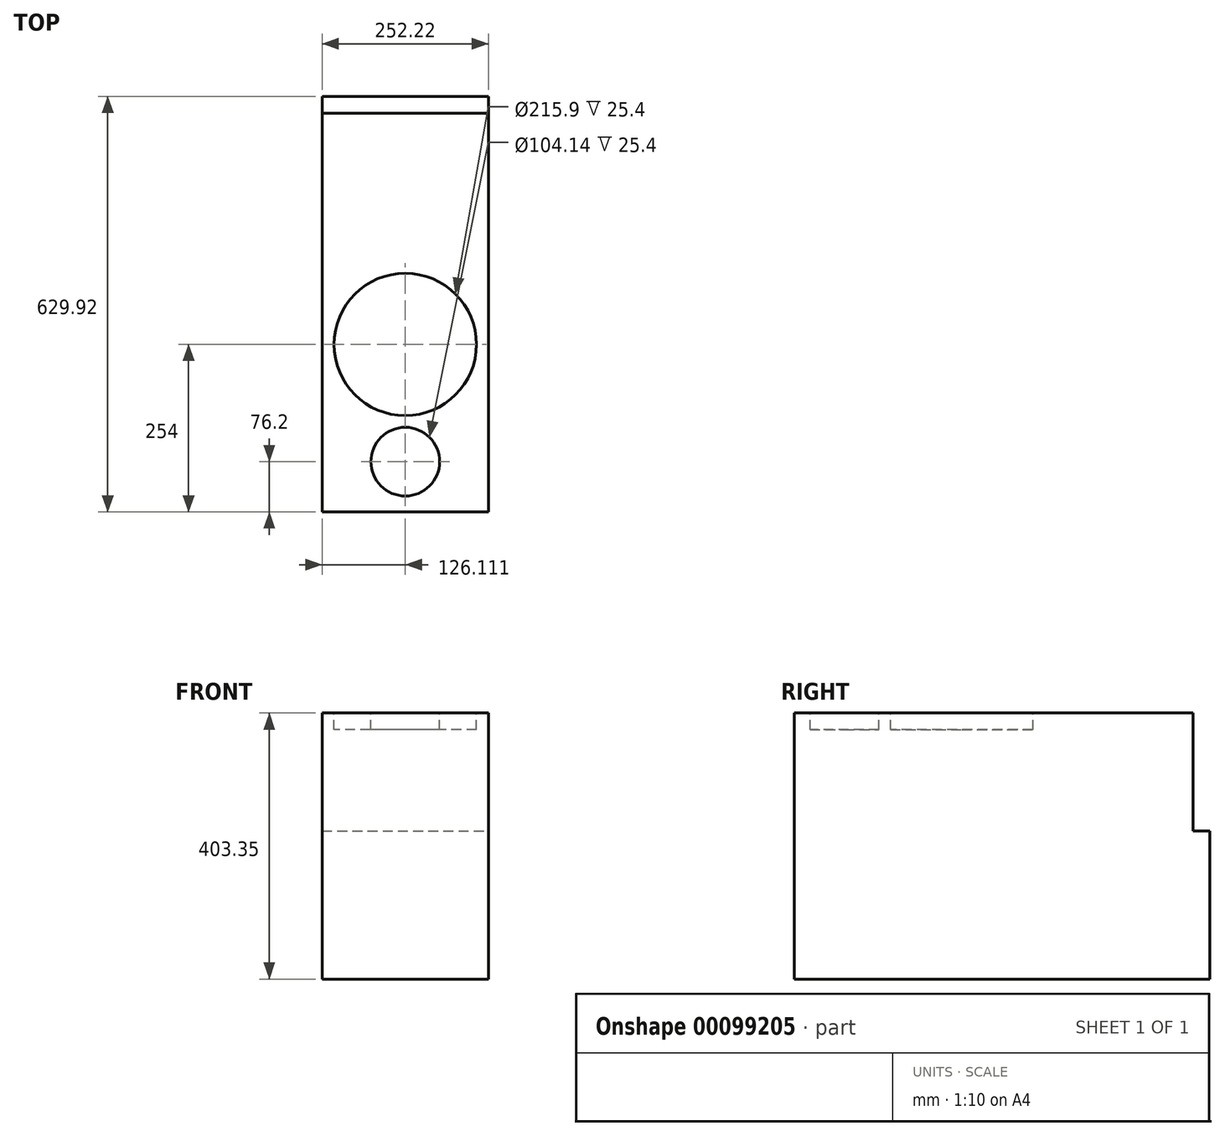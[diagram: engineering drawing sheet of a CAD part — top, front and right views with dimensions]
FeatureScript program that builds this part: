
annotation { "Feature Type Name" : "Feature", "Feature Type Description" : "" }
export const myFeature = defineFeature(function(context is Context, id is Id, definition is map)
    precondition{}
    {
        {
            var Q0;
            Q0=qCreatedBy(makeId("Front.planeOp"),FACE);
            var sketch = newSketch(context, id + "F0", { "sketchPlane" : qUnion([Q0])});
            skLineSegment(sketch, "E0.bottom", {"start": v(0, 0) * mm, "end": v(252.22, 0) * mm});
            skLineSegment(sketch, "E0.top", {"start": v(0, 403.35) * mm, "end": v(252.22, 403.35) * mm});
            skLineSegment(sketch, "E0.left", {"start": v(0, 0) * mm, "end": v(0, 403.35) * mm});
            skLineSegment(sketch, "E0.right", {"start": v(252.22, 0) * mm, "end": v(252.22, 403.35) * mm});
            skSolve(sketch);
        }
        {
            var Q0;
            Q0=makeQuery(id+"F0.imprint","IMPRINT",FACE,{"disambiguationData":[TD([[makeQuery(id+"F0.imprint","IMPRINT",EDGE,{"derivedFrom":sQuery(id+"F0.wireOp",EDGE,"E0.bottom")}),1.0]])]});
            extrude(context, id + "F1", {"entities" : qUnion([Q0]), "depth" : 629.92 * mm});
        }
        {
            var Q0;
            Q0=makeQuery(id+"F1.opExtrude","SWEPT_FACE",FACE,{"disambiguationData":[OSD([sQuery(id+"F0.wireOp",EDGE,"E0.top")])]});
            var sketch = newSketch(context, id + "F2", { "sketchPlane" : qUnion([Q0])});
            skCircle(sketch, "E1", {"center": v(126.11, -375.92) * mm, "radius": 107.95 * mm});
            skLineSegment(sketch, "E2", {"start": v(126.11, 0) * mm, "end": v(126.11, -375.92) * mm, "construction": true});
            skLineSegment(sketch, "E3", {"start": v(126.11, -375.92) * mm, "end": v(126.11, -553.72) * mm, "construction": true});
            skLineSegment(sketch, "E4.0", {"start": v(0, -629.92) * mm, "end": v(0, 0) * mm});
            skCircle(sketch, "E5", {"center": v(126.11, -553.72) * mm, "radius": 52.07 * mm});
            skSolve(sketch);
        }
        {
            var Q0;
            Q0=makeQuery(id+"F2.imprint","IMPRINT",FACE,{"disambiguationData":[TD([[makeQuery(id+"F2.imprint","IMPRINT",EDGE,{"derivedFrom":sQuery(id+"F2.wireOp",EDGE,"E5")}),1.0]])]});
            var Q1;
            Q1=makeQuery(id+"F2.imprint","IMPRINT",FACE,{"disambiguationData":[TD([[makeQuery(id+"F2.imprint","IMPRINT",EDGE,{"derivedFrom":sQuery(id+"F2.wireOp",EDGE,"E1")}),1.0]])]});
            extrude(context, id + "F3", {"entities" : qUnion([Q0, Q1]), "operationType" : NewBodyOperationType.REMOVE, "oppositeDirection" : true, "depth" : 25.4 * mm});
        }
        {
            var Q0;
            Q0=makeQuery(id+"F1.opExtrude","SWEPT_FACE",FACE,{"disambiguationData":[OSD([sQuery(id+"F0.wireOp",EDGE,"E0.top")])]});
            var sketch = newSketch(context, id + "F4", { "sketchPlane" : qUnion([Q0])});
            skSolve(sketch);
        }
        {
            var Q0;
            {var subQ0=sQuery(id+"F0.wireOp",EDGE,"E0.top");Q0=makeQuery(id+"F4.imprint","IMPRINT",FACE,{"disambiguationData":[TD([[makeQuery(id+"F4.imprint","IMPRINT",EDGE,{"derivedFrom":makeQuery(id+"F1.opExtrude","CAP_EDGE",EDGE,{"disambiguationData":[OSD([subQ0])],"isStart":true})}),-1.0]])]});}
            var sketch = newSketch(context, id + "F5", { "sketchPlane" : qUnion([Q0])});
            skLineSegment(sketch, "E6.0", {"start": v(252.22, -25.4) * mm, "end": v(252.22, 0) * mm});
            skLineSegment(sketch, "E7.0", {"start": v(0, -25.4) * mm, "end": v(0, 0) * mm});
            skLineSegment(sketch, "E8", {"start": v(252.22, -25.4) * mm, "end": v(0, -25.4) * mm});
            skLineSegment(sketch, "E9", {"start": v(252.22, 0) * mm, "end": v(0, 0) * mm});
            skPoint(sketch, "E10.orphan", {"position": v(0, -629.92) * mm});
            skPoint(sketch, "E11.orphan", {"position": v(252.22, -629.92) * mm});
            skPoint(sketch, "E12.orphan", {"position": v(252.22, 0) * mm});
            skPoint(sketch, "E13.orphan", {"position": v(0, 0) * mm});
            skSolve(sketch);
        }
        {
            var Q0;
            Q0=makeQuery(id+"F5.imprint","IMPRINT",FACE,{"disambiguationData":[TD([[makeQuery(id+"F5.imprint","IMPRINT",EDGE,{"derivedFrom":sQuery(id+"F5.wireOp",EDGE,"E6.0")}),1.0]])]});
            extrude(context, id + "F6", {"entities" : qUnion([Q0]), "operationType" : NewBodyOperationType.REMOVE, "oppositeDirection" : true, "depth" : 178.82 * mm});
        }
    });
